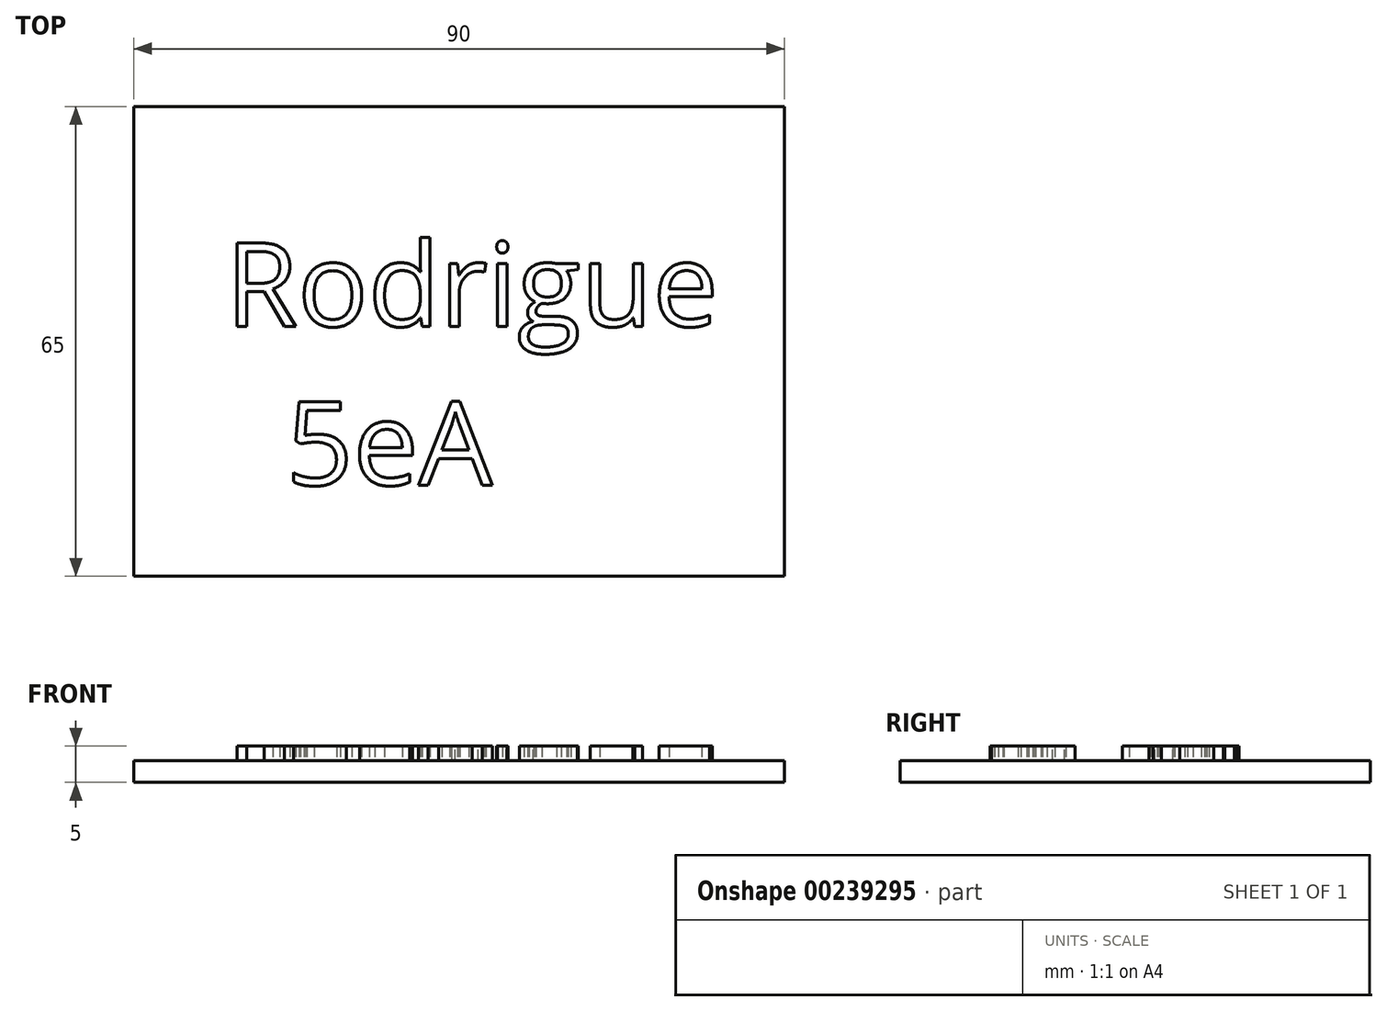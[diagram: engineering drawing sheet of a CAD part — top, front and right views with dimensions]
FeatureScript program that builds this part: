
annotation { "Feature Type Name" : "Feature", "Feature Type Description" : "" }
export const myFeature = defineFeature(function(context is Context, id is Id, definition is map)
    precondition{}
    {
        {
            var Q0;
            Q0=qCreatedBy(makeId("Top.planeOp"),FACE);
            var sketch = newSketch(context, id + "F0", { "sketchPlane" : qUnion([Q0])});
            skLineSegment(sketch, "E0.bottom", {"start": v(0, 0) * mm, "end": v(90, 0) * mm});
            skLineSegment(sketch, "E0.top", {"start": v(0, -65) * mm, "end": v(90, -65) * mm});
            skLineSegment(sketch, "E0.left", {"start": v(0, 0) * mm, "end": v(0, -65) * mm});
            skLineSegment(sketch, "E0.right", {"start": v(90, 0) * mm, "end": v(90, -65) * mm});
            skSolve(sketch);
        }
        {
            var Q0;
            Q0=makeQuery(id+"F0.imprint","IMPRINT",FACE,{"disambiguationData":[TD([[makeQuery(id+"F0.imprint","IMPRINT",EDGE,{"derivedFrom":sQuery(id+"F0.wireOp",EDGE,"E0.bottom")}),-1.0]])]});
            extrude(context, id + "F1", {"entities" : qUnion([Q0]), "depth" : 3 * mm});
        }
        {
            var Q0;
            Q0=makeQuery(id+"F1.opExtrude","CAP_FACE",FACE,{"disambiguationData":[OSD([sQuery(id+"F0.wireOp",EDGE,"E0.bottom"),sQuery(id+"F0.wireOp",EDGE,"E0.top"),sQuery(id+"F0.wireOp",EDGE,"E0.left"),sQuery(id+"F0.wireOp",EDGE,"E0.right")])],"isStart":false});
            var sketch = newSketch(context, id + "F2", { "sketchPlane" : qUnion([Q0])});
            skText(sketch, "E1", { "text": "Rodrigue\n  5eA", "fontName": "OpenSans-Regular.ttf"});
            const initialGuessF2  = {"E1": [0.0127, -0.03041, 1, 0, 0.01163]};
            skSetInitialGuess(sketch, initialGuessF2);
            skSolve(sketch);
        }
        {
            var Q0;
            Q0 = qSketchRegion(id + "F2", true);
            extrude(context, id + "F3", {"entities" : qUnion([Q0]), "operationType" : NewBodyOperationType.ADD, "depth" : 2 * mm});
        }
        {
            var Q0;
            Q0 = qSketchRegion(id + "F2", true);
            extrude(context, id + "F4", {"entities" : qUnion([Q0]), "operationType" : NewBodyOperationType.ADD, "depth" : 2 * mm});
        }
    });
